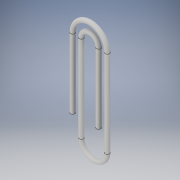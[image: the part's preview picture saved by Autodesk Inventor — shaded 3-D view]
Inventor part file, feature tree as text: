
AUTODESK INVENTOR PART (.ipt)
format: ipt  version: 2018 (Build 220112000, 112)  size: 135,168 bytes
history: native  units: in
note: dims shown in document units (in); Inventor stores cm internally (conversion verified against a paired STEP export)
features: sketch x2, plane x1, sweep x1
ambient origin geometry x8: Origin, YZ Plane, XZ Plane, XY Plane, X Axis, Y Axis, Z Axis, Center Point
bodies: Solid1 (feature_tree)
feature tree (4):
  sketch  "Sketch1"  dims[d0=1.0in d1=1.25in]
  plane  "Work Plane1"
  sweep  "Sweep1"
  sketch  "Sketch2"  dims[d2=0.125in d3=0.25in d4=0.125in d5=0.0625in d6=0.0in d7=0.0in]
